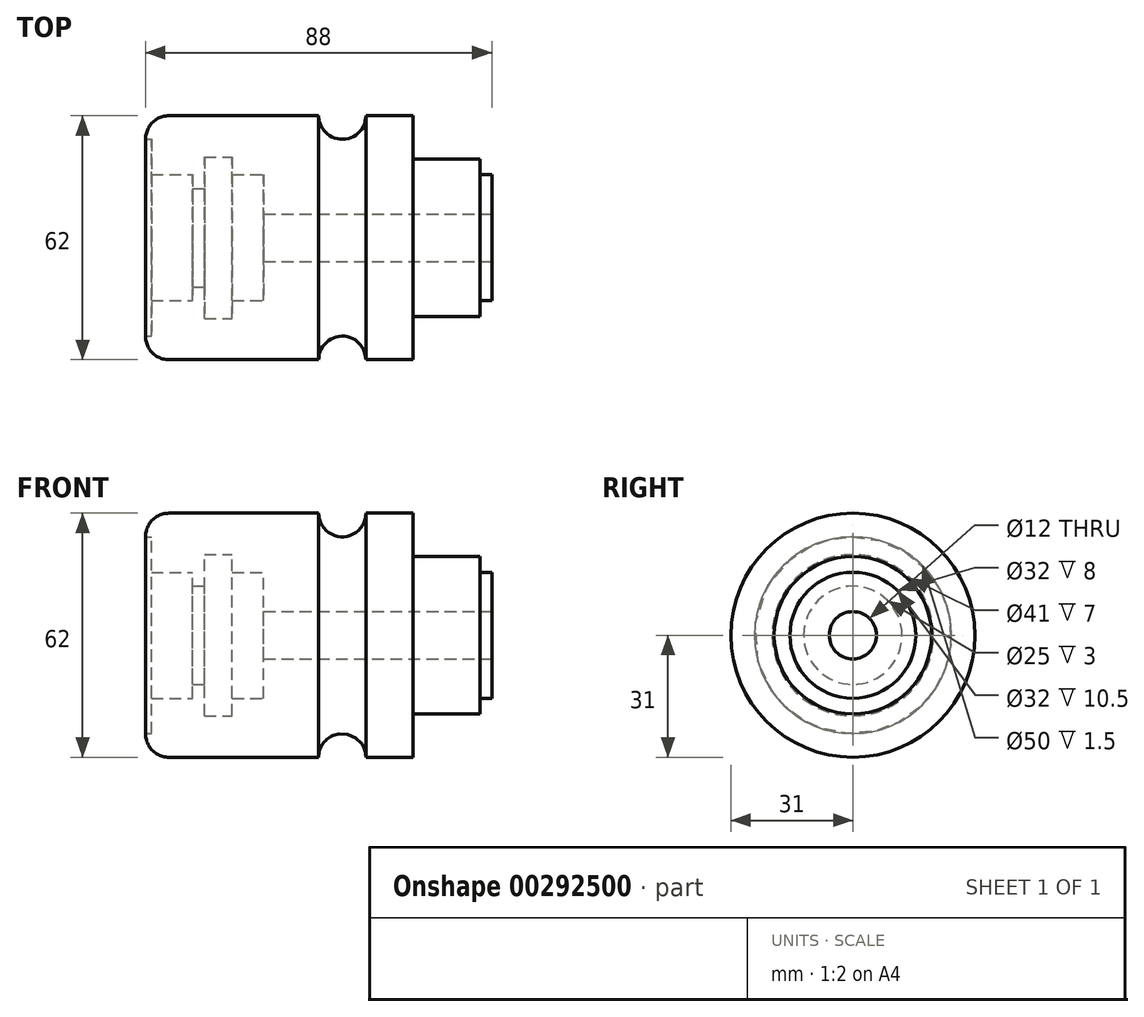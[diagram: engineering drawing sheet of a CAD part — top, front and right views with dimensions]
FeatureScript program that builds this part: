
annotation { "Feature Type Name" : "Feature", "Feature Type Description" : "" }
export const myFeature = defineFeature(function(context is Context, id is Id, definition is map)
    precondition{}
    {
        {
            var Q0;
            Q0=qCreatedBy(makeId("Front.planeOp"),FACE);
            var sketch = newSketch(context, id + "F0", { "sketchPlane" : qUnion([Q0])});
            skLineSegment(sketch, "E0", {"start": v(0, 0) * mm, "end": v(111.24, 0) * mm, "construction": true});
            skLineSegment(sketch, "E1", {"start": v(0, 0) * mm, "end": v(0, 31) * mm});
            skLineSegment(sketch, "E2", {"start": v(0, 31) * mm, "end": v(44, 31) * mm});
            skLineSegment(sketch, "E3", {"start": v(68, 31) * mm, "end": v(68, 20) * mm});
            skLineSegment(sketch, "E4", {"start": v(68, 20) * mm, "end": v(85, 20) * mm});
            skLineSegment(sketch, "E5", {"start": v(85, 20) * mm, "end": v(85, 16) * mm});
            skLineSegment(sketch, "E6", {"start": v(85, 16) * mm, "end": v(88, 16) * mm});
            skLineSegment(sketch, "E7", {"start": v(88, 16) * mm, "end": v(88, 0) * mm});
            skLineSegment(sketch, "E8", {"start": v(88, 0) * mm, "end": v(0, 0) * mm});
            skArc(sketch, "E9", {"start": v(44, 31) * mm, "mid": v(50, 25) * mm, "end": v(56, 31) * mm});
            skLineSegment(sketch, "E10.trimOffspring", {"start": v(56, 31) * mm, "end": v(68, 31) * mm});
            skSolve(sketch);
        }
        {
            var Q0;
            Q0=makeQuery(id+"F0.imprint","IMPRINT",FACE,{"disambiguationData":[TD([[makeQuery(id+"F0.imprint","IMPRINT",EDGE,{"derivedFrom":sQuery(id+"F0.wireOp",EDGE,"E1")}),-1.0]])]});
            var Q1;
            Q1=sQuery(id+"F0.wireOp",EDGE,"E0");
            revolve(context, id + "F1", {"entities" : qUnion([Q0]), "axis" : qUnion([Q1]), "revolveType" : RevolveType.FULL});
        }
        {
            var Q0;
            Q0=qCreatedBy(makeId("Front.planeOp"),FACE);
            var sketch = newSketch(context, id + "F2", { "sketchPlane" : qUnion([Q0])});
            skLineSegment(sketch, "E11", {"start": v(0, 0) * mm, "end": v(0, 25) * mm});
            skLineSegment(sketch, "E12", {"start": v(0, 25) * mm, "end": v(1.5, 25) * mm});
            skLineSegment(sketch, "E13", {"start": v(1.5, 25) * mm, "end": v(1.5, 16) * mm});
            skLineSegment(sketch, "E14", {"start": v(1.5, 16) * mm, "end": v(12, 16) * mm});
            skLineSegment(sketch, "E15", {"start": v(12, 16) * mm, "end": v(12, 12.5) * mm});
            skLineSegment(sketch, "E16", {"start": v(12, 12.5) * mm, "end": v(15, 12.5) * mm});
            skLineSegment(sketch, "E17", {"start": v(15, 12.5) * mm, "end": v(15, 20.5) * mm});
            skLineSegment(sketch, "E18", {"start": v(15, 20.5) * mm, "end": v(22, 20.5) * mm});
            skLineSegment(sketch, "E19", {"start": v(22, 20.5) * mm, "end": v(22, 16) * mm});
            skLineSegment(sketch, "E20", {"start": v(22, 16) * mm, "end": v(30, 16) * mm});
            skLineSegment(sketch, "E21", {"start": v(30, 16) * mm, "end": v(30, 6) * mm});
            skLineSegment(sketch, "E22", {"start": v(30, 6) * mm, "end": v(88, 6) * mm});
            skLineSegment(sketch, "E23", {"start": v(88, 6) * mm, "end": v(88, 0) * mm});
            skLineSegment(sketch, "E24", {"start": v(88, 0) * mm, "end": v(0, 0) * mm});
            skLineSegment(sketch, "E25", {"start": v(0, 0) * mm, "end": v(-25.3, 0) * mm, "construction": true});
            skSolve(sketch);
        }
        {
            var Q0;
            Q0 = qSketchRegion(id + "F2", true);
            var Q1;
            Q1=sQuery(id+"F2.wireOp",EDGE,"E25");
            revolve(context, id + "F3", {"operationType" : NewBodyOperationType.REMOVE, "entities" : qUnion([Q0]), "axis" : qUnion([Q1]), "revolveType" : RevolveType.FULL});
        }
        {
            var Q0;
            Q0=makeQuery(id+"F1.opRevolve","SWEPT_EDGE",EDGE,{"disambiguationData":[OSD([sQuery(id+"F0.wireOp",EDGE,"E1"),sQuery(id+"F0.wireOp",EDGE,"E2")])]});
            fillet(context, id + "F4", {"entities" : qUnion([Q0]), "radius" : 6 * mm, "tangentPropagation" : true, "allowEdgeOverflow" : false});
        }
    });
